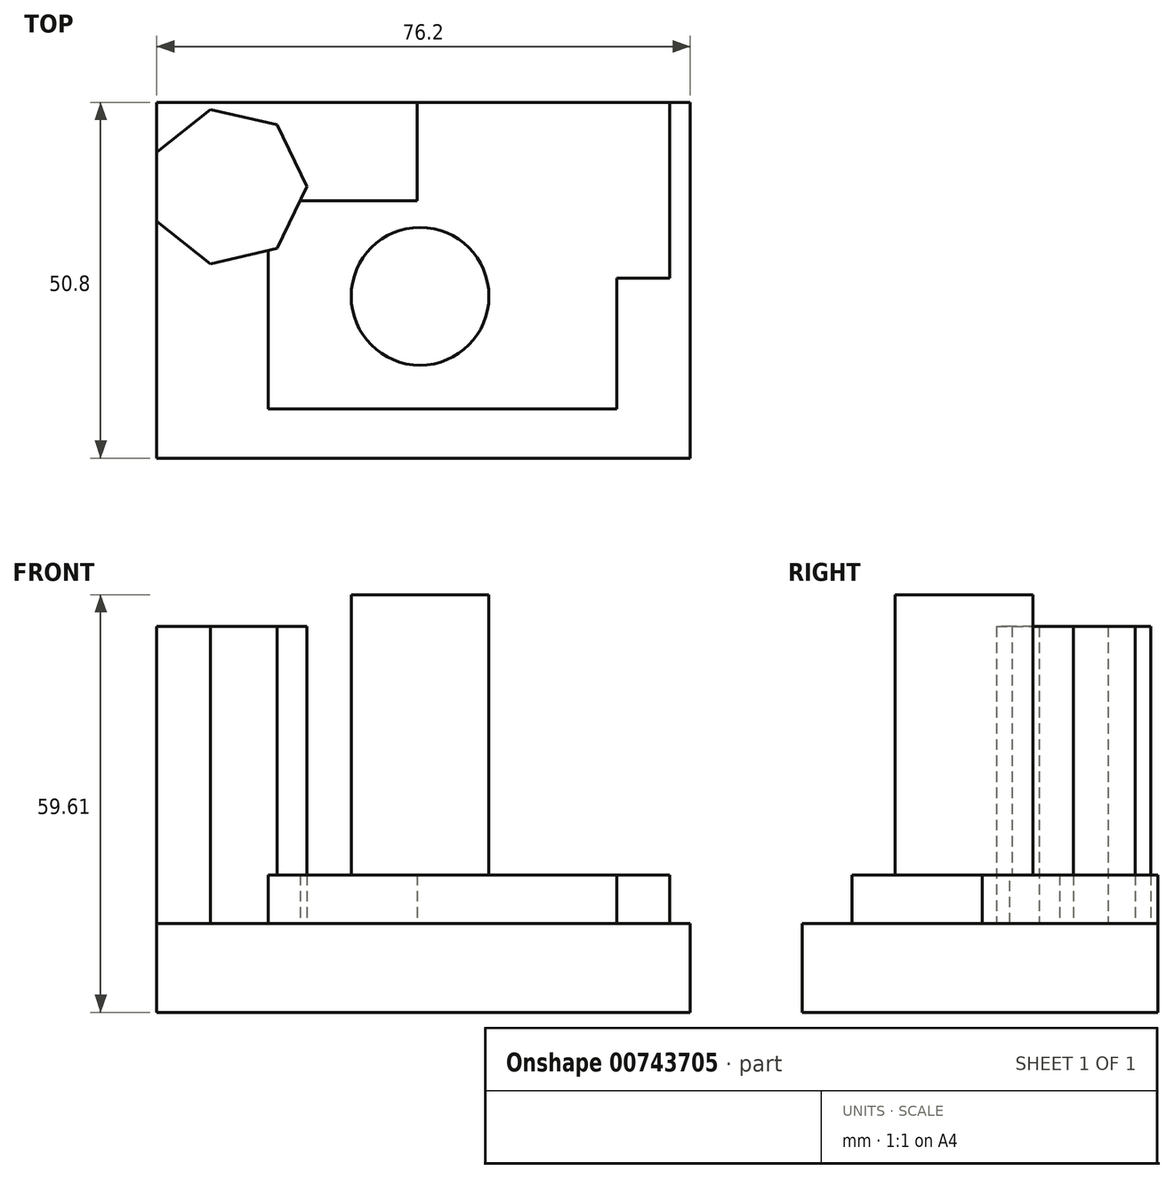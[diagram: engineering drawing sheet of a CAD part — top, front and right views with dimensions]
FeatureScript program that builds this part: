
annotation { "Feature Type Name" : "Feature", "Feature Type Description" : "" }
export const myFeature = defineFeature(function(context is Context, id is Id, definition is map)
    precondition{}
    {
        {
            var Q0;
            Q0=qCreatedBy(makeId("Top.planeOp"),FACE);
            var sketch = newSketch(context, id + "F0", { "sketchPlane" : qUnion([Q0])});
            skLineSegment(sketch, "E0.bottom", {"start": v(0, -163.01) * mm, "end": v(-76.2, -163.01) * mm});
            skLineSegment(sketch, "E0.top", {"start": v(0, -213.81) * mm, "end": v(-76.2, -213.81) * mm});
            skLineSegment(sketch, "E0.left", {"start": v(0, -163.01) * mm, "end": v(0, -213.81) * mm});
            skLineSegment(sketch, "E0.right", {"start": v(-76.2, -163.01) * mm, "end": v(-76.2, -213.81) * mm});
            skSolve(sketch);
        }
        {
            var Q0;
            Q0=makeQuery(id+"F0.imprint","IMPRINT",FACE,{"disambiguationData":[TD([[makeQuery(id+"F0.imprint","IMPRINT",EDGE,{"derivedFrom":sQuery(id+"F0.wireOp",EDGE,"E0.bottom")}),1.0]])]});
            extrude(context, id + "F1", {"entities" : qUnion([Q0]), "oppositeDirection" : true, "depth" : 12.7 * mm, "offsetDistance" : 25.4 * mm});
        }
        {
            var Q0;
            Q0=makeQuery(id+"F1.opExtrude","CAP_FACE",FACE,{"disambiguationData":[OSD([sQuery(id+"F0.wireOp",EDGE,"E0.bottom"),sQuery(id+"F0.wireOp",EDGE,"E0.top"),sQuery(id+"F0.wireOp",EDGE,"E0.left"),sQuery(id+"F0.wireOp",EDGE,"E0.right")])],"isStart":true});
            var sketch = newSketch(context, id + "F2", { "sketchPlane" : qUnion([Q0])});
            skLineSegment(sketch, "E1.bottom", {"start": v(-60.28, -192.13) * mm, "end": v(-10.52, -192.13) * mm});
            skLineSegment(sketch, "E1.top", {"start": v(-60.28, -177.04) * mm, "end": v(-10.52, -177.04) * mm});
            skLineSegment(sketch, "E1.left", {"start": v(-60.28, -192.13) * mm, "end": v(-60.28, -177.04) * mm});
            skLineSegment(sketch, "E1.right", {"start": v(-10.52, -192.13) * mm, "end": v(-10.52, -177.04) * mm});
            skLineSegment(sketch, "E2.bottom", {"start": v(-60.28, -206.74) * mm, "end": v(-10.52, -206.74) * mm});
            skLineSegment(sketch, "E2.left", {"start": v(-60.28, -206.74) * mm, "end": v(-60.28, -192.13) * mm});
            skLineSegment(sketch, "E2.right", {"start": v(-10.52, -206.74) * mm, "end": v(-10.52, -192.13) * mm});
            skLineSegment(sketch, "E3.bottom", {"start": v(-39, -188.12) * mm, "end": v(-2.96, -188.12) * mm});
            skLineSegment(sketch, "E3.top", {"start": v(-39, -147.12) * mm, "end": v(-2.96, -147.12) * mm});
            skLineSegment(sketch, "E3.left", {"start": v(-39, -188.12) * mm, "end": v(-39, -147.12) * mm});
            skLineSegment(sketch, "E3.right", {"start": v(-2.96, -188.12) * mm, "end": v(-2.96, -147.12) * mm});
            skSolve(sketch);
        }
        {
            var Q0;
            Q0=makeQuery(id+"F2.imprint","IMPRINT",FACE,{"disambiguationData":[TD([[makeQuery(id+"F2.imprint","IMPRINT",EDGE,{"derivedFrom":sQuery(id+"F2.wireOp",EDGE,"E2.bottom")}),1.0]])]});
            var Q1;
            {var subQ4=sQuery(id+"F2.wireOp",EDGE,"E1.left");Q1=makeQuery(id+"F2.imprint","IMPRINT",FACE,{"disambiguationData":[TD([[makeQuery(id+"F2.imprint","IMPRINT",EDGE,{"derivedFrom":subQ4}),-1.0]])]});}
            var Q2;
            {var subQ0=sQuery(id+"F2.wireOp",EDGE,"E1.right");var subQ1=sQuery(id+"F2.wireOp",EDGE,"E1.top");var subQ2=makeQuery(id+"F2.imprint","INTERSECT",VERTEX,{"derivedFrom":[subQ1,subQ0]});Q2=makeQuery(id+"F2.imprint","IMPRINT",FACE,{"disambiguationData":[TD([[makeQuery(id+"F2.imprint","IMPRINT",EDGE,{"disambiguationData":[TD([[subQ2,1.0]])],"derivedFrom":subQ1}),-1.0]])]});}
            var Q3;
            {var subQ1=sQuery(id+"F2.wireOp",EDGE,"E1.top");var subQ8=sQuery(id+"F2.wireOp",EDGE,"E1.right");var subQ10=makeQuery(id+"F2.imprint","INTERSECT",VERTEX,{"derivedFrom":[subQ1,subQ8]});Q3=makeQuery(id+"F2.imprint","IMPRINT",FACE,{"disambiguationData":[TD([[makeQuery(id+"F2.imprint","IMPRINT",EDGE,{"disambiguationData":[TD([[subQ10,1.0]])],"derivedFrom":subQ1}),1.0]])]});}
            extrude(context, id + "F3", {"entities" : qUnion([Q0, Q1, Q2, Q3]), "operationType" : NewBodyOperationType.ADD, "depth" : 6.92 * mm, "offsetDistance" : 25.4 * mm});
        }
        {
            var Q0;
            Q0=makeQuery(id+"F3.opExtrude","CAP_FACE",FACE,{"disambiguationData":[OSD([sQuery(id+"F0.wireOp",EDGE,"E0.bottom"),sQuery(id+"F2.wireOp",EDGE,"E1.top"),sQuery(id+"F2.wireOp",EDGE,"E1.left"),sQuery(id+"F2.wireOp",EDGE,"E1.right"),sQuery(id+"F2.wireOp",EDGE,"E2.bottom"),sQuery(id+"F2.wireOp",EDGE,"E2.left"),sQuery(id+"F2.wireOp",EDGE,"E2.right"),sQuery(id+"F2.wireOp",EDGE,"E3.bottom"),sQuery(id+"F2.wireOp",EDGE,"E3.left"),sQuery(id+"F2.wireOp",EDGE,"E3.right")])],"isStart":false});
            var sketch = newSketch(context, id + "F4", { "sketchPlane" : qUnion([Q0])});
            skCircle(sketch, "E4", {"center": v(-38.6, -190.7) * mm, "radius": 9.84 * mm});
            skSolve(sketch);
        }
        {
            var Q0;
            Q0 = qSketchRegion(id + "F4", true);
            extrude(context, id + "F5", {"entities" : qUnion([Q0]), "operationType" : NewBodyOperationType.ADD, "depth" : 40 * mm, "offsetDistance" : 25.4 * mm});
        }
        {
            var Q0;
            Q0=makeQuery(id+"F1.opExtrude","CAP_FACE",FACE,{"disambiguationData":[OSD([sQuery(id+"F0.wireOp",EDGE,"E0.bottom"),sQuery(id+"F0.wireOp",EDGE,"E0.top"),sQuery(id+"F0.wireOp",EDGE,"E0.left"),sQuery(id+"F0.wireOp",EDGE,"E0.right")])],"isStart":true});
            var sketch = newSketch(context, id + "F6", { "sketchPlane" : qUnion([Q0])});
            skCircle(sketch, "E5.cCircle", {"center": v(-66.03, -175.06) * mm, "radius": 10.17 * mm, "construction": true});
            skLineSegment(sketch, "E5.0", {"start": v(-76.2, -179.95) * mm, "end": v(-76.2, -170.16) * mm});
            skLineSegment(sketch, "E5.1", {"start": v(-76.2, -170.16) * mm, "end": v(-68.54, -164.05) * mm});
            skLineSegment(sketch, "E5.2", {"start": v(-68.54, -164.05) * mm, "end": v(-59, -166.23) * mm});
            skLineSegment(sketch, "E5.3", {"start": v(-59, -166.23) * mm, "end": v(-54.74, -175.06) * mm});
            skLineSegment(sketch, "E5.4", {"start": v(-54.74, -175.06) * mm, "end": v(-59, -183.88) * mm});
            skLineSegment(sketch, "E5.5", {"start": v(-59, -183.88) * mm, "end": v(-68.54, -186.06) * mm});
            skLineSegment(sketch, "E5.6", {"start": v(-68.54, -186.06) * mm, "end": v(-76.2, -179.95) * mm});
            skPoint(sketch, "E5.0.midPoint", {"position": v(-76.2, -175.06) * mm});
            skSolve(sketch);
        }
        {
            var Q0;
            Q0 = qSketchRegion(id + "F6", true);
            extrude(context, id + "F7", {"entities" : qUnion([Q0]), "operationType" : NewBodyOperationType.ADD, "depth" : 42.38 * mm, "offsetDistance" : 25.4 * mm});
        }
    });
